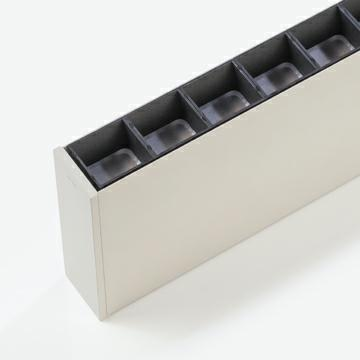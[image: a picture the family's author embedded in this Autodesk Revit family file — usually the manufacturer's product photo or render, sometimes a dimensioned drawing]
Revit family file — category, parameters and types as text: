
# Revit family: KKDC_General_KOH40-H_HighPower_3000K_1140mm
name_source: partatom
category: 조명 설비
units: mm (PartAtom-declared; Revit-internal decimal feet)

## family parameters
OmniClass 번호 = 23.80.70.11
OmniClass 제목 = Luminaries for Internal Lighting
공유 = 아니오
광원 = 예
로드될 때 보이드를 사용하여 절단 = 아니오
룸 계산 점 = 아니오
부품 유형 = 배선함
원형 커넥터 치수 = 지름 사용
주석 방향 유지 = 아니오
항상 수직 = 예
호스트 = 천장

## types (5) — shared parameters
감광 램프 색상 온도 변화 = <없음>
경사도 = 90.00°
기본 높이 = 0 mm
램프 = KOH HighPower
렌더링 시 발산 모양 표시 = 예
색상 필터 = 16777215
와티지 해설 = DIR 67W / IND 65W
유형 이미지 = 5ba8ae69eb1dd.jpg
직사각형 길이에서 발산 = 1,130 mm
직사각형 폭에서 발산 = 40 mm

## per-type parameters (varying)
| type | 측광 웹 파일 |
| KOH40-H HighPower 3000K Louvre 10deg 1140mm | KOH40-H (DIR) Louvre 10deg No Cover.IES |
| KOH40-H HighPower 3000K Louvre 20deg 1140mm | KOH40-H (DIR) Louvre 20deg No Cover.IES |
| KOH40-H HighPower 3000K Louvre 30deg 1140mm | KOH40-H (DIR) Louvre 30deg No Cover.IES |
| KOH40-H HighPower 3000K Louvre Spread 1140mm | KOH40-H (DIR) Louvre Spread No Cover.IES |
| KOH40-H HighPower 3000K Louvre Frosted 1140mm | KOH40-H (DIR) Louvre Frosted Cover.IES |
